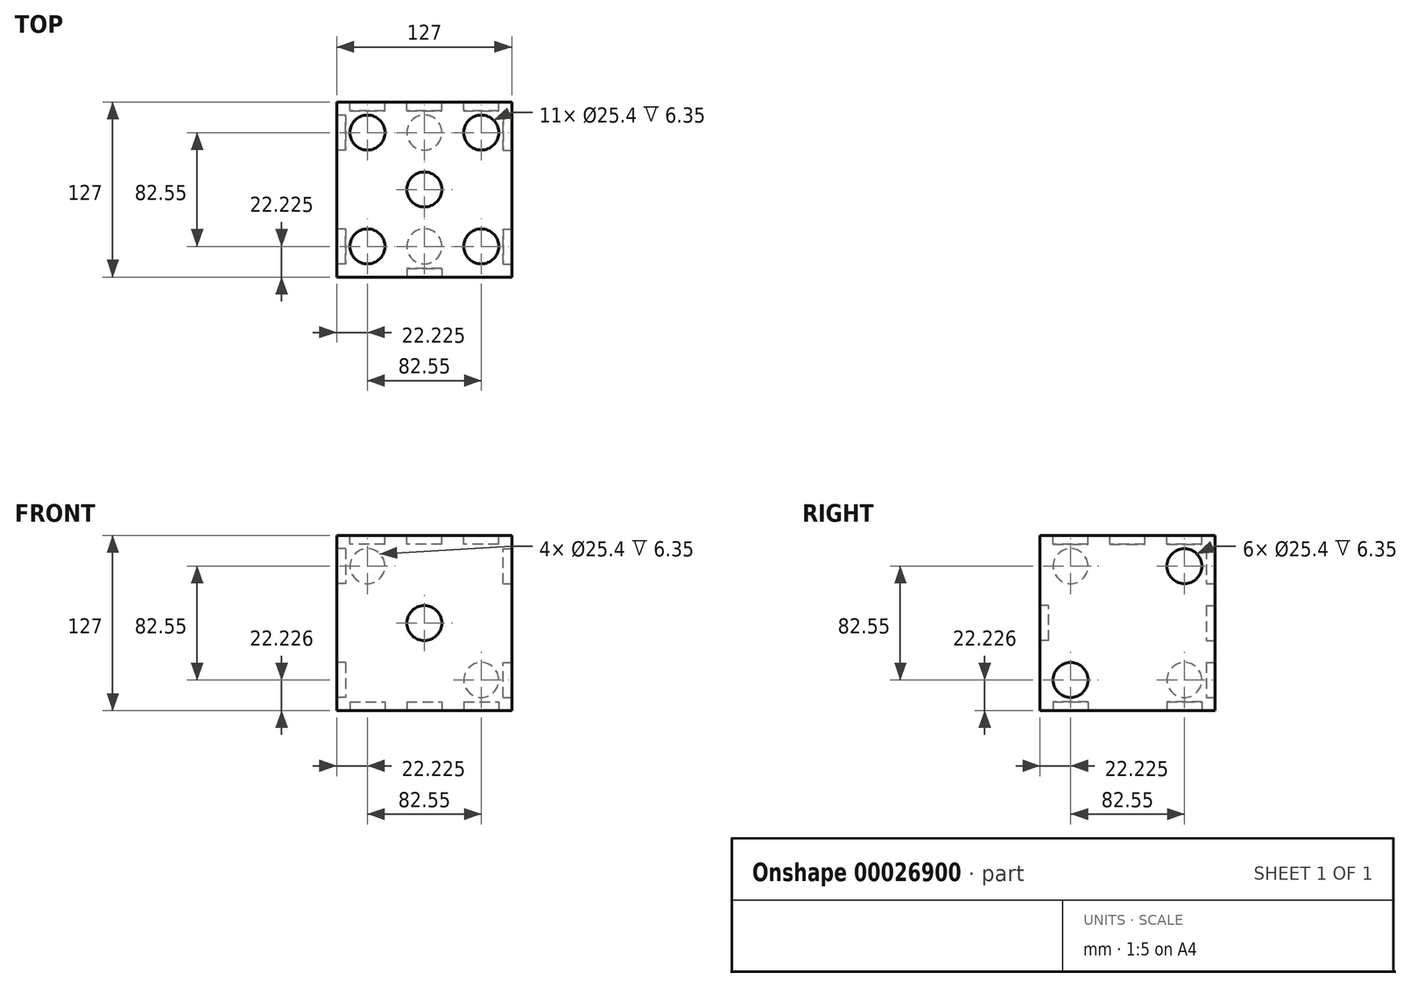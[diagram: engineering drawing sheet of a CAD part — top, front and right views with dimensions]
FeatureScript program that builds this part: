
annotation { "Feature Type Name" : "Feature", "Feature Type Description" : "" }
export const myFeature = defineFeature(function(context is Context, id is Id, definition is map)
    precondition{}
    {
        {
            var Q0;
            Q0=qCreatedBy(makeId("Front.planeOp"),FACE);
            var sketch = newSketch(context, id + "F0", { "sketchPlane" : qUnion([Q0])});
            skLineSegment(sketch, "E0.bottom", {"start": v(-74.6, -0.64) * mm, "end": v(52.4, -0.64) * mm});
            skLineSegment(sketch, "E0.top", {"start": v(-74.6, 126.36) * mm, "end": v(52.4, 126.36) * mm});
            skLineSegment(sketch, "E0.left", {"start": v(-74.6, -0.64) * mm, "end": v(-74.6, 126.36) * mm});
            skLineSegment(sketch, "E0.right", {"start": v(52.4, -0.64) * mm, "end": v(52.4, 126.36) * mm});
            skSolve(sketch);
        }
        {
            var Q0;
            Q0 = qSketchRegion(id + "F0", true);
            extrude(context, id + "F1", {"entities" : qUnion([Q0]), "flatOperationType" : FlatOperationType.REMOVE, "thickness1" : 6.35 * mm, "thickness2" : 0 * mm, "thickness" : 6.35 * mm, "offsetDistance" : 25.4 * mm, "startOffsetBound" : StartOffsetType.BLIND, "startOffsetDistance" : 25.4 * mm, "depth" : 127 * mm, "domain" : OperationDomain.MODEL});
        }
        {
            var Q0;
            Q0=makeQuery(id+"F1.opExtrude","CAP_FACE",FACE,{"disambiguationData":[OSD([sQuery(id+"F0.wireOp",EDGE,"E0.bottom"),sQuery(id+"F0.wireOp",EDGE,"E0.top"),sQuery(id+"F0.wireOp",EDGE,"E0.left"),sQuery(id+"F0.wireOp",EDGE,"E0.right")])],"isStart":false});
            var sketch = newSketch(context, id + "F2", { "sketchPlane" : qUnion([Q0]), "disableImprinting" : false});
            skCircle(sketch, "E1", {"center": v(-11.1, 62.86) * mm, "radius": 12.7 * mm});
            skSolve(sketch);
        }
        {
            var Q0;
            Q0=makeQuery(id+"F1.opExtrude","SWEPT_FACE",FACE,{"disambiguationData":[OSD([sQuery(id+"F0.wireOp",EDGE,"E0.right")])]});
            var sketch = newSketch(context, id + "F3", { "sketchPlane" : qUnion([Q0])});
            skCircle(sketch, "E2", {"center": v(-104.78, 21.59) * mm, "radius": 12.7 * mm});
            skCircle(sketch, "E3", {"center": v(-22.23, 104.14) * mm, "radius": 12.7 * mm});
            skSolve(sketch);
        }
        {
            var Q0;
            Q0 = qSketchRegion(id + "F3", true);
            extrude(context, id + "F4", {"entities" : qUnion([Q0]), "operationType" : NewBodyOperationType.REMOVE, "oppositeDirection" : true, "depth" : 6.35 * mm});
        }
        {
            var Q0;
            Q0=makeQuery(id+"F2.imprint","IMPRINT",FACE,{"disambiguationData":[TD([[makeQuery(id+"F2.imprint","IMPRINT",EDGE,{"derivedFrom":sQuery(id+"F2.wireOp",EDGE,"E1")}),1.0]])]});
            extrude(context, id + "F5", {"entities" : qUnion([Q0]), "operationType" : NewBodyOperationType.REMOVE, "flatOperationType" : FlatOperationType.REMOVE, "thickness1" : 6.35 * mm, "thickness2" : 0 * mm, "thickness" : 6.35 * mm, "oppositeDirection" : true, "offsetDistance" : 25.4 * mm, "startOffsetBound" : StartOffsetType.BLIND, "startOffsetDistance" : 25.4 * mm, "depth" : 6.35 * mm, "domain" : OperationDomain.MODEL});
        }
        {
            var Q0;
            Q0=makeQuery(id+"F1.opExtrude","CAP_FACE",FACE,{"disambiguationData":[OSD([sQuery(id+"F0.wireOp",EDGE,"E0.bottom"),sQuery(id+"F0.wireOp",EDGE,"E0.top"),sQuery(id+"F0.wireOp",EDGE,"E0.left"),sQuery(id+"F0.wireOp",EDGE,"E0.right")])],"isStart":true});
            var sketch = newSketch(context, id + "F6", { "sketchPlane" : qUnion([Q0])});
            skCircle(sketch, "E4", {"center": v(-30.18, 21.59) * mm, "radius": 12.7 * mm});
            skCircle(sketch, "E5", {"center": v(11.1, 62.86) * mm, "radius": 12.7 * mm});
            skCircle(sketch, "E6", {"center": v(52.37, 104.14) * mm, "radius": 12.7 * mm});
            skSolve(sketch);
        }
        {
            var Q0;
            Q0 = qSketchRegion(id + "F6", true);
            extrude(context, id + "F7", {"entities" : qUnion([Q0]), "operationType" : NewBodyOperationType.REMOVE, "oppositeDirection" : true, "depth" : 6.35 * mm});
        }
        {
            var Q0;
            Q0=makeQuery(id+"F1.opExtrude","SWEPT_FACE",FACE,{"disambiguationData":[OSD([sQuery(id+"F0.wireOp",EDGE,"E0.left")])]});
            var sketch = newSketch(context, id + "F8", { "sketchPlane" : qUnion([Q0])});
            skCircle(sketch, "E7", {"center": v(22.23, 21.59) * mm, "radius": 12.7 * mm});
            skCircle(sketch, "E8", {"center": v(22.22, 104.14) * mm, "radius": 12.7 * mm});
            skCircle(sketch, "E9", {"center": v(104.78, 104.14) * mm, "radius": 12.7 * mm});
            skCircle(sketch, "E10", {"center": v(104.78, 21.59) * mm, "radius": 12.7 * mm});
            skSolve(sketch);
        }
        {
            var Q0;
            Q0 = qSketchRegion(id + "F8", true);
            extrude(context, id + "F9", {"entities" : qUnion([Q0]), "operationType" : NewBodyOperationType.REMOVE, "oppositeDirection" : true, "depth" : 6.35 * mm});
        }
        {
            var Q0;
            Q0=makeQuery(id+"F1.opExtrude","SWEPT_FACE",FACE,{"disambiguationData":[OSD([sQuery(id+"F0.wireOp",EDGE,"E0.top")])]});
            var sketch = newSketch(context, id + "F10", { "sketchPlane" : qUnion([Q0])});
            skCircle(sketch, "E11", {"center": v(30.18, -22.22) * mm, "radius": 12.7 * mm});
            skCircle(sketch, "E12", {"center": v(30.18, -104.78) * mm, "radius": 12.7 * mm});
            skCircle(sketch, "E13", {"center": v(-52.37, -104.78) * mm, "radius": 12.7 * mm});
            skCircle(sketch, "E14", {"center": v(-52.37, -22.22) * mm, "radius": 12.7 * mm});
            skCircle(sketch, "E15", {"center": v(-11.1, -63.5) * mm, "radius": 12.7 * mm});
            skSolve(sketch);
        }
        {
            var Q0;
            Q0 = qSketchRegion(id + "F10", true);
            extrude(context, id + "F11", {"entities" : qUnion([Q0]), "operationType" : NewBodyOperationType.REMOVE, "oppositeDirection" : true, "depth" : 6.35 * mm});
        }
        {
            var Q0;
            Q0=makeQuery(id+"F1.opExtrude","SWEPT_FACE",FACE,{"disambiguationData":[OSD([sQuery(id+"F0.wireOp",EDGE,"E0.bottom")])]});
            var sketch = newSketch(context, id + "F12", { "sketchPlane" : qUnion([Q0])});
            skCircle(sketch, "E16", {"center": v(-52.37, 104.78) * mm, "radius": 12.7 * mm});
            skCircle(sketch, "E17", {"center": v(-52.37, 22.23) * mm, "radius": 12.7 * mm});
            skCircle(sketch, "E18", {"center": v(-11.1, 22.22) * mm, "radius": 12.7 * mm});
            skCircle(sketch, "E19", {"center": v(30.18, 22.22) * mm, "radius": 12.7 * mm});
            skCircle(sketch, "E20", {"center": v(-11.1, 104.78) * mm, "radius": 12.7 * mm});
            skCircle(sketch, "E21", {"center": v(30.18, 104.78) * mm, "radius": 12.7 * mm});
            skSolve(sketch);
        }
        {
            var Q0;
            Q0 = qSketchRegion(id + "F12", true);
            extrude(context, id + "F13", {"entities" : qUnion([Q0]), "operationType" : NewBodyOperationType.REMOVE, "oppositeDirection" : true, "depth" : 6.35 * mm});
        }
    });
